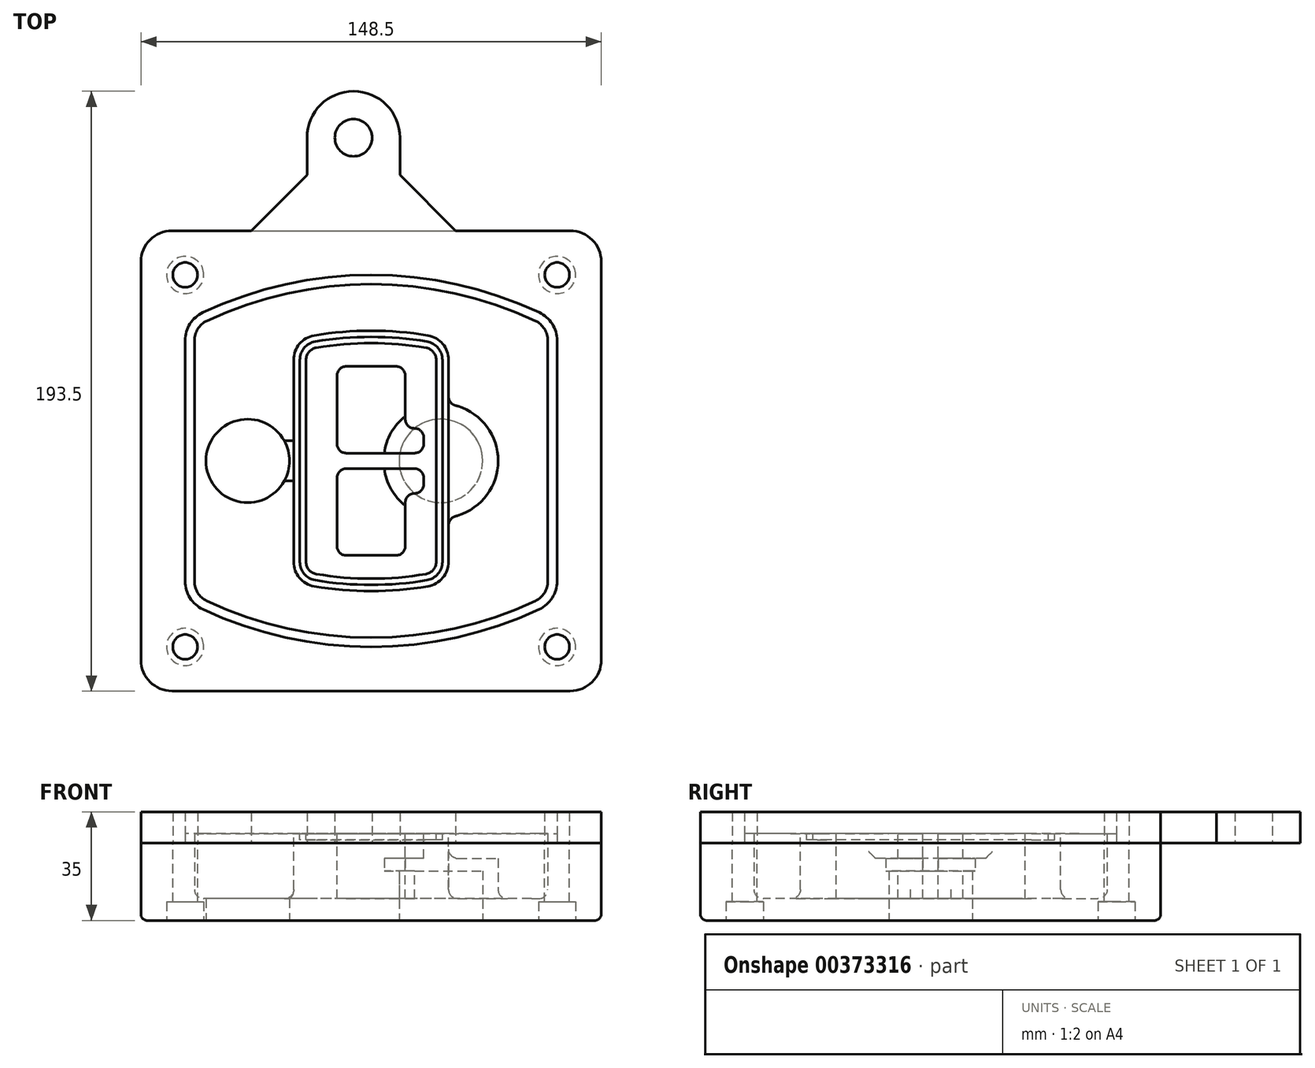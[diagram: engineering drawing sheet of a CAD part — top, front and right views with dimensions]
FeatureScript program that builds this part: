
annotation { "Feature Type Name" : "Feature", "Feature Type Description" : "" }
export const myFeature = defineFeature(function(context is Context, id is Id, definition is map)
    precondition{}
    {
        {
            var Q0;
            Q0=qCreatedBy(makeId("Top.planeOp"),FACE);
            var sketch = newSketch(context, id + "F0", { "sketchPlane" : qUnion([Q0])});
            skPoint(sketch, "E0.rect.middle", {"position": v(0, 0) * mm});
            skLineSegment(sketch, "E1.bottom", {"start": v(-64.25, -74.25) * mm, "end": v(64.25, -74.25) * mm});
            skLineSegment(sketch, "E1.top", {"start": v(-64.25, 74.25) * mm, "end": v(64.25, 74.25) * mm});
            skLineSegment(sketch, "E1.left", {"start": v(-74.25, -64.25) * mm, "end": v(-74.25, 64.25) * mm});
            skLineSegment(sketch, "E1.right", {"start": v(74.25, -64.25) * mm, "end": v(74.25, 64.25) * mm});
            skLineSegment(sketch, "E2", {"start": v(-74.25, 74.25) * mm, "end": v(74.25, -74.25) * mm, "construction": true});
            skLineSegment(sketch, "E3", {"start": v(74.25, 74.25) * mm, "end": v(-74.25, -74.25) * mm, "construction": true});
            skCircle(sketch, "E4", {"center": v(-60, 60) * mm, "radius": 4 * mm});
            skCircle(sketch, "E5", {"center": v(60, 60) * mm, "radius": 4 * mm});
            skCircle(sketch, "E6", {"center": v(60, -60) * mm, "radius": 4 * mm});
            skCircle(sketch, "E7", {"center": v(-60, -60) * mm, "radius": 4 * mm});
            skLineSegment(sketch, "E8", {"start": v(-60, 60) * mm, "end": v(60, 60) * mm, "construction": true});
            skLineSegment(sketch, "E9", {"start": v(60, 60) * mm, "end": v(60, -60) * mm, "construction": true});
            skLineSegment(sketch, "E10", {"start": v(60, -60) * mm, "end": v(-60, -60) * mm, "construction": true});
            skLineSegment(sketch, "E11", {"start": v(-60, -60) * mm, "end": v(-60, 60) * mm, "construction": true});
            skLineSegment(sketch, "E12", {"start": v(-60, 38.83) * mm, "end": v(-60, -38.83) * mm});
            skLineSegment(sketch, "E13", {"start": v(60, 38.83) * mm, "end": v(60, -38.83) * mm});
            skArc(sketch, "E14", {"start": v(54.26, 47.88) * mm, "mid": v(0, 60) * mm, "end": v(-54.26, 47.88) * mm});
            skArc(sketch, "E15", {"start": v(-54.26, -47.88) * mm, "mid": v(0, -60) * mm, "end": v(54.26, -47.88) * mm});
            skLineSegment(sketch, "E16", {"start": v(-60, 0) * mm, "end": v(60, 0) * mm, "construction": true});
            skPoint(sketch, "E17.visualSharp", {"position": v(-60, -45) * mm});
            skArc(sketch, "E17.filletArc", {"start": v(-60, -38.83) * mm, "mid": v(-58.44, -44.2) * mm, "end": v(-54.26, -47.88) * mm});
            skPoint(sketch, "E18.visualSharp", {"position": v(-60, 45) * mm});
            skArc(sketch, "E18.filletArc", {"start": v(-54.26, 47.88) * mm, "mid": v(-58.44, 44.2) * mm, "end": v(-60, 38.83) * mm});
            skPoint(sketch, "E19.visualSharp", {"position": v(60, 45) * mm});
            skArc(sketch, "E19.filletArc", {"start": v(60, 38.83) * mm, "mid": v(58.44, 44.2) * mm, "end": v(54.26, 47.88) * mm});
            skPoint(sketch, "E20.visualSharp", {"position": v(60, -45) * mm});
            skArc(sketch, "E20.filletArc", {"start": v(54.26, -47.88) * mm, "mid": v(58.44, -44.2) * mm, "end": v(60, -38.83) * mm});
            skPoint(sketch, "E21.visualSharp", {"position": v(-74.25, 74.25) * mm});
            skArc(sketch, "E21.filletArc", {"start": v(-64.25, 74.25) * mm, "mid": v(-71.32, 71.32) * mm, "end": v(-74.25, 64.25) * mm});
            skPoint(sketch, "E22.visualSharp", {"position": v(74.25, 74.25) * mm});
            skArc(sketch, "E22.filletArc", {"start": v(74.25, 64.25) * mm, "mid": v(71.32, 71.32) * mm, "end": v(64.25, 74.25) * mm});
            skPoint(sketch, "E23.visualSharp", {"position": v(74.25, -74.25) * mm});
            skArc(sketch, "E23.filletArc", {"start": v(64.25, -74.25) * mm, "mid": v(71.32, -71.32) * mm, "end": v(74.25, -64.25) * mm});
            skPoint(sketch, "E24.visualSharp", {"position": v(-74.25, -74.25) * mm});
            skArc(sketch, "E24.filletArc", {"start": v(-74.25, -64.25) * mm, "mid": v(-71.32, -71.32) * mm, "end": v(-64.25, -74.25) * mm});
            skArc(sketch, "E25.0", {"start": v(57, 38.83) * mm, "mid": v(55.9, 42.58) * mm, "end": v(52.98, 45.17) * mm});
            skLineSegment(sketch, "E25.1", {"start": v(57, 38.83) * mm, "end": v(57, -38.83) * mm});
            skArc(sketch, "E25.2", {"start": v(52.98, -45.17) * mm, "mid": v(55.9, -42.58) * mm, "end": v(57, -38.83) * mm});
            skArc(sketch, "E25.3", {"start": v(-52.98, -45.17) * mm, "mid": v(0, -57) * mm, "end": v(52.98, -45.17) * mm});
            skArc(sketch, "E25.4", {"start": v(-57, -38.83) * mm, "mid": v(-55.9, -42.58) * mm, "end": v(-52.98, -45.17) * mm});
            skArc(sketch, "E25.5", {"start": v(52.98, 45.17) * mm, "mid": v(0, 57) * mm, "end": v(-52.98, 45.17) * mm});
            skLineSegment(sketch, "E25.6", {"start": v(-57, 38.83) * mm, "end": v(-57, -38.83) * mm});
            skArc(sketch, "E25.7", {"start": v(-52.98, 45.17) * mm, "mid": v(-55.9, 42.58) * mm, "end": v(-57, 38.83) * mm});
            skArc(sketch, "E26.0", {"start": v(-55.96, 51.5) * mm, "mid": v(-61.82, 46.33) * mm, "end": v(-64, 38.83) * mm});
            skArc(sketch, "E26.1", {"start": v(55.96, 51.5) * mm, "mid": v(0, 64) * mm, "end": v(-55.96, 51.5) * mm});
            skArc(sketch, "E26.2", {"start": v(64, 38.83) * mm, "mid": v(61.82, 46.33) * mm, "end": v(55.96, 51.5) * mm});
            skLineSegment(sketch, "E26.3", {"start": v(64, 38.83) * mm, "end": v(64, -38.83) * mm});
            skArc(sketch, "E26.4", {"start": v(55.96, -51.5) * mm, "mid": v(61.82, -46.33) * mm, "end": v(64, -38.83) * mm});
            skLineSegment(sketch, "E26.5", {"start": v(-64, 38.83) * mm, "end": v(-64, -38.83) * mm});
            skArc(sketch, "E26.6", {"start": v(-55.96, -51.5) * mm, "mid": v(0, -64) * mm, "end": v(55.96, -51.5) * mm});
            skArc(sketch, "E26.7", {"start": v(-64, -38.83) * mm, "mid": v(-61.82, -46.33) * mm, "end": v(-55.96, -51.5) * mm});
            skSolve(sketch);
        }
        {
            var Q0;
            Q0=makeQuery(id+"F0.imprint","IMPRINT",FACE,{"disambiguationData":[TD([[makeQuery(id+"F0.imprint","IMPRINT",EDGE,{"derivedFrom":sQuery(id+"F0.wireOp",EDGE,"E1.bottom")}),1.0]])]});
            var Q1;
            Q1=makeQuery(id+"F0.imprint","IMPRINT",FACE,{"disambiguationData":[TD([[makeQuery(id+"F0.imprint","IMPRINT",EDGE,{"derivedFrom":sQuery(id+"F0.wireOp",EDGE,"E12")}),1.0]])]});
            var Q2;
            Q2=makeQuery(id+"F0.imprint","IMPRINT",FACE,{"disambiguationData":[TD([[makeQuery(id+"F0.imprint","IMPRINT",EDGE,{"derivedFrom":sQuery(id+"F0.wireOp",EDGE,"E25.0")}),1.0]])]});
            var Q3;
            Q3=makeQuery(id+"F0.imprint","IMPRINT",FACE,{"disambiguationData":[TD([[makeQuery(id+"F0.imprint","IMPRINT",EDGE,{"derivedFrom":sQuery(id+"F0.wireOp",EDGE,"E12")}),-1.0]])]});
            extrude(context, id + "F1", {"entities" : qUnion([Q0, Q1, Q2, Q3]), "oppositeDirection" : true, "depth" : 25 * mm});
        }
        {
            var Q0;
            Q0=makeQuery(id+"F0.imprint","IMPRINT",FACE,{"disambiguationData":[TD([[makeQuery(id+"F0.imprint","IMPRINT",EDGE,{"derivedFrom":sQuery(id+"F0.wireOp",EDGE,"E12")}),1.0]])]});
            extrude(context, id + "F2", {"entities" : qUnion([Q0]), "operationType" : NewBodyOperationType.ADD, "depth" : 3 * mm});
        }
        {
            var Q0;
            Q0=makeQuery(id+"F0.imprint","IMPRINT",FACE,{"disambiguationData":[TD([[makeQuery(id+"F0.imprint","IMPRINT",EDGE,{"derivedFrom":sQuery(id+"F0.wireOp",EDGE,"E25.0")}),1.0]])]});
            extrude(context, id + "F3", {"entities" : qUnion([Q0]), "operationType" : NewBodyOperationType.REMOVE, "oppositeDirection" : true, "depth" : 18 * mm});
        }
        {
            var Q0;
            Q0=makeQuery(id+"F2.opExtrude","CAP_FACE",FACE,{"disambiguationData":[OSD([sQuery(id+"F0.wireOp",EDGE,"E12"),sQuery(id+"F0.wireOp",EDGE,"E13"),sQuery(id+"F0.wireOp",EDGE,"E14"),sQuery(id+"F0.wireOp",EDGE,"E15"),sQuery(id+"F0.wireOp",EDGE,"E17.filletArc"),sQuery(id+"F0.wireOp",EDGE,"E18.filletArc"),sQuery(id+"F0.wireOp",EDGE,"E19.filletArc"),sQuery(id+"F0.wireOp",EDGE,"E20.filletArc"),sQuery(id+"F0.wireOp",EDGE,"E25.0"),sQuery(id+"F0.wireOp",EDGE,"E25.1"),sQuery(id+"F0.wireOp",EDGE,"E25.2"),sQuery(id+"F0.wireOp",EDGE,"E25.3"),sQuery(id+"F0.wireOp",EDGE,"E25.4"),sQuery(id+"F0.wireOp",EDGE,"E25.5"),sQuery(id+"F0.wireOp",EDGE,"E25.6"),sQuery(id+"F0.wireOp",EDGE,"E25.7")])],"isStart":false});
            var sketch = newSketch(context, id + "F4", { "sketchPlane" : qUnion([Q0])});
            skArc(sketch, "E27.0", {"start": v(-18.34, -40.45) * mm, "mid": v(0, -42) * mm, "end": v(18.34, -40.45) * mm});
            skArc(sketch, "E28.0", {"start": v(18.34, 40.45) * mm, "mid": v(0, 42) * mm, "end": v(-18.34, 40.45) * mm});
            skLineSegment(sketch, "E29", {"start": v(-25, 32.57) * mm, "end": v(-25, -32.57) * mm});
            skLineSegment(sketch, "E30", {"start": v(25, 32.57) * mm, "end": v(25, -32.57) * mm});
            skLineSegment(sketch, "E31", {"start": v(-25, 39.1) * mm, "end": v(25, 39.1) * mm, "construction": true});
            skLineSegment(sketch, "E32", {"start": v(-25, -39.1) * mm, "end": v(25, -39.1) * mm, "construction": true});
            skPoint(sketch, "E33.visualSharp", {"position": v(-25, 39.1) * mm});
            skArc(sketch, "E33.filletArc", {"start": v(-18.34, 40.45) * mm, "mid": v(-23.11, 37.73) * mm, "end": v(-25, 32.57) * mm});
            skPoint(sketch, "E34.visualSharp", {"position": v(25, 39.1) * mm});
            skArc(sketch, "E34.filletArc", {"start": v(25, 32.57) * mm, "mid": v(23.11, 37.73) * mm, "end": v(18.34, 40.45) * mm});
            skPoint(sketch, "E35.visualSharp", {"position": v(25, -39.1) * mm});
            skArc(sketch, "E35.filletArc", {"start": v(18.34, -40.45) * mm, "mid": v(23.11, -37.73) * mm, "end": v(25, -32.57) * mm});
            skPoint(sketch, "E36.visualSharp", {"position": v(-25, -39.1) * mm});
            skArc(sketch, "E36.filletArc", {"start": v(-25, -32.57) * mm, "mid": v(-23.11, -37.73) * mm, "end": v(-18.34, -40.45) * mm});
            skArc(sketch, "E37.0", {"start": v(52.98, 45.17) * mm, "mid": v(0, 57) * mm, "end": v(-52.98, 45.17) * mm});
            skArc(sketch, "E37.1", {"start": v(-52.98, 45.17) * mm, "mid": v(-55.9, 42.58) * mm, "end": v(-57, 38.83) * mm});
            skLineSegment(sketch, "E37.2", {"start": v(-57, 38.83) * mm, "end": v(-57, -38.83) * mm});
            skArc(sketch, "E37.3", {"start": v(-57, -38.83) * mm, "mid": v(-55.9, -42.58) * mm, "end": v(-52.98, -45.17) * mm});
            skArc(sketch, "E37.4", {"start": v(-52.98, -45.17) * mm, "mid": v(0, -57) * mm, "end": v(52.98, -45.17) * mm});
            skArc(sketch, "E37.5", {"start": v(52.98, -45.17) * mm, "mid": v(55.9, -42.58) * mm, "end": v(57, -38.83) * mm});
            skLineSegment(sketch, "E37.6", {"start": v(57, 38.83) * mm, "end": v(57, -38.83) * mm});
            skArc(sketch, "E37.7", {"start": v(57, 38.83) * mm, "mid": v(55.9, 42.58) * mm, "end": v(52.98, 45.17) * mm});
            skLineSegment(sketch, "E38.0", {"start": v(23, 32.57) * mm, "end": v(23, -32.57) * mm});
            skArc(sketch, "E38.1", {"start": v(18, -38.48) * mm, "mid": v(21.58, -36.44) * mm, "end": v(23, -32.57) * mm});
            skArc(sketch, "E38.2", {"start": v(-18, -38.48) * mm, "mid": v(0, -40) * mm, "end": v(18, -38.48) * mm});
            skArc(sketch, "E38.3", {"start": v(-23, -32.57) * mm, "mid": v(-21.58, -36.44) * mm, "end": v(-18, -38.48) * mm});
            skLineSegment(sketch, "E38.4", {"start": v(-23, 32.57) * mm, "end": v(-23, -32.57) * mm});
            skArc(sketch, "E38.5", {"start": v(23, 32.57) * mm, "mid": v(21.58, 36.44) * mm, "end": v(18, 38.48) * mm});
            skArc(sketch, "E38.6", {"start": v(-18, 38.48) * mm, "mid": v(-21.58, 36.44) * mm, "end": v(-23, 32.57) * mm});
            skArc(sketch, "E38.7", {"start": v(18, 38.48) * mm, "mid": v(0, 40) * mm, "end": v(-18, 38.48) * mm});
            skArc(sketch, "E39.0", {"start": v(21, 32.57) * mm, "mid": v(20.06, 35.15) * mm, "end": v(17.67, 36.5) * mm});
            skLineSegment(sketch, "E39.1", {"start": v(21, 32.57) * mm, "end": v(21, -32.57) * mm});
            skArc(sketch, "E39.2", {"start": v(17.67, -36.5) * mm, "mid": v(20.06, -35.15) * mm, "end": v(21, -32.57) * mm});
            skArc(sketch, "E39.3", {"start": v(-17.67, -36.5) * mm, "mid": v(0, -38) * mm, "end": v(17.67, -36.5) * mm});
            skArc(sketch, "E39.4", {"start": v(-21, -32.57) * mm, "mid": v(-20.06, -35.15) * mm, "end": v(-17.67, -36.5) * mm});
            skArc(sketch, "E39.5", {"start": v(17.67, 36.5) * mm, "mid": v(0, 38) * mm, "end": v(-17.67, 36.5) * mm});
            skLineSegment(sketch, "E39.6", {"start": v(-21, 32.57) * mm, "end": v(-21, -32.57) * mm});
            skArc(sketch, "E39.7", {"start": v(-17.67, 36.5) * mm, "mid": v(-20.06, 35.15) * mm, "end": v(-21, 32.57) * mm});
            skLineSegment(sketch, "E40", {"start": v(-25, 0) * mm, "end": v(25, 0) * mm, "construction": true});
            skLineSegment(sketch, "E41", {"start": v(-11, 5.5) * mm, "end": v(-11, 27.5) * mm});
            skLineSegment(sketch, "E42", {"start": v(-8, 30.5) * mm, "end": v(8, 30.5) * mm});
            skLineSegment(sketch, "E43", {"start": v(11, 27.5) * mm, "end": v(11, 13.5) * mm});
            skLineSegment(sketch, "E44", {"start": v(14, 10.5) * mm, "end": v(14, 10.5) * mm});
            skLineSegment(sketch, "E45", {"start": v(17, 7.5) * mm, "end": v(17, 5.5) * mm});
            skLineSegment(sketch, "E46", {"start": v(14, 2.5) * mm, "end": v(-8, 2.5) * mm});
            skPoint(sketch, "E47.visualSharp", {"position": v(-11, 30.5) * mm});
            skArc(sketch, "E47.filletArc", {"start": v(-8, 30.5) * mm, "mid": v(-10.12, 29.62) * mm, "end": v(-11, 27.5) * mm});
            skPoint(sketch, "E48.visualSharp", {"position": v(11, 30.5) * mm});
            skArc(sketch, "E48.filletArc", {"start": v(11, 27.5) * mm, "mid": v(10.12, 29.62) * mm, "end": v(8, 30.5) * mm});
            skPoint(sketch, "E49.visualSharp", {"position": v(11, 10.5) * mm});
            skArc(sketch, "E49.filletArc", {"start": v(11, 13.5) * mm, "mid": v(11.88, 11.38) * mm, "end": v(14, 10.5) * mm});
            skPoint(sketch, "E50.visualSharp", {"position": v(17, 10.5) * mm});
            skArc(sketch, "E50.filletArc", {"start": v(17, 7.5) * mm, "mid": v(16.12, 9.62) * mm, "end": v(14, 10.5) * mm});
            skPoint(sketch, "E51.visualSharp", {"position": v(17, 2.5) * mm});
            skArc(sketch, "E51.filletArc", {"start": v(14, 2.5) * mm, "mid": v(16.12, 3.38) * mm, "end": v(17, 5.5) * mm});
            skPoint(sketch, "E52.visualSharp", {"position": v(-11, 2.5) * mm});
            skArc(sketch, "E52.filletArc", {"start": v(-11, 5.5) * mm, "mid": v(-10.12, 3.38) * mm, "end": v(-8, 2.5) * mm});
            skLineSegment(sketch, "E53.0.MirrorCS", {"start": v(14, -2.5) * mm, "end": v(-8, -2.5) * mm});
            skArc(sketch, "E54.0.MirrorCS", {"start": v(-11, -5.5) * mm, "mid": v(-10.12, -3.38) * mm, "end": v(-8, -2.5) * mm});
            skLineSegment(sketch, "E55.0.MirrorCS", {"start": v(-11, -5.5) * mm, "end": v(-11, -27.5) * mm});
            skArc(sketch, "E56.0.MirrorCS", {"start": v(-8, -30.5) * mm, "mid": v(-10.12, -29.62) * mm, "end": v(-11, -27.5) * mm});
            skLineSegment(sketch, "E57.0.MirrorCS", {"start": v(-8, -30.5) * mm, "end": v(8, -30.5) * mm});
            skArc(sketch, "E58.0.MirrorCS", {"start": v(11, -27.5) * mm, "mid": v(10.12, -29.62) * mm, "end": v(8, -30.5) * mm});
            skLineSegment(sketch, "E59.0.MirrorCS", {"start": v(11, -27.5) * mm, "end": v(11, -13.5) * mm});
            skArc(sketch, "E60.0.MirrorCS", {"start": v(11, -13.5) * mm, "mid": v(11.88, -11.38) * mm, "end": v(14, -10.5) * mm});
            skArc(sketch, "E61.0.MirrorCS", {"start": v(17, -7.5) * mm, "mid": v(16.12, -9.62) * mm, "end": v(14, -10.5) * mm});
            skLineSegment(sketch, "E62.0.MirrorCS", {"start": v(17, -7.5) * mm, "end": v(17, -5.5) * mm});
            skArc(sketch, "E63.0.MirrorCS", {"start": v(14, -2.5) * mm, "mid": v(16.12, -3.38) * mm, "end": v(17, -5.5) * mm});
            skSolve(sketch);
        }
        {
            var Q0;
            Q0=makeQuery(id+"F4.imprint","IMPRINT",FACE,{"disambiguationData":[TD([[makeQuery(id+"F4.imprint","IMPRINT",EDGE,{"derivedFrom":sQuery(id+"F4.wireOp",EDGE,"E27.0")}),1.0]])]});
            var Q1;
            Q1=makeQuery(id+"F4.imprint","IMPRINT",FACE,{"disambiguationData":[TD([[makeQuery(id+"F4.imprint","IMPRINT",EDGE,{"derivedFrom":sQuery(id+"F4.wireOp",EDGE,"E38.0")}),-1.0]])]});
            var Q2;
            Q2=makeQuery(id+"F4.imprint","IMPRINT",FACE,{"disambiguationData":[TD([[makeQuery(id+"F4.imprint","IMPRINT",EDGE,{"derivedFrom":sQuery(id+"F4.wireOp",EDGE,"E39.0")}),1.0]])]});
            extrude(context, id + "F5", {"entities" : qUnion([Q0, Q1, Q2]), "operationType" : NewBodyOperationType.ADD, "endBound" : BoundingType.UP_TO_NEXT, "oppositeDirection" : true, "depth" : 25 * mm});
        }
        {
            var Q0;
            Q0=makeQuery(id+"F4.imprint","IMPRINT",FACE,{"disambiguationData":[TD([[makeQuery(id+"F4.imprint","IMPRINT",EDGE,{"derivedFrom":sQuery(id+"F4.wireOp",EDGE,"E38.0")}),-1.0]])]});
            extrude(context, id + "F6", {"entities" : qUnion([Q0]), "operationType" : NewBodyOperationType.REMOVE, "oppositeDirection" : true, "depth" : 2 * mm});
        }
        {
            var Q0;
            Q0=makeQuery(id+"F1.opExtrude","CAP_FACE",FACE,{"disambiguationData":[OSD([sQuery(id+"F0.wireOp",EDGE,"E1.bottom"),sQuery(id+"F0.wireOp",EDGE,"E1.top"),sQuery(id+"F0.wireOp",EDGE,"E1.left"),sQuery(id+"F0.wireOp",EDGE,"E1.right"),sQuery(id+"F0.wireOp",EDGE,"E4"),sQuery(id+"F0.wireOp",EDGE,"E5"),sQuery(id+"F0.wireOp",EDGE,"E6"),sQuery(id+"F0.wireOp",EDGE,"E7"),sQuery(id+"F0.wireOp",EDGE,"E21.filletArc"),sQuery(id+"F0.wireOp",EDGE,"E22.filletArc"),sQuery(id+"F0.wireOp",EDGE,"E23.filletArc"),sQuery(id+"F0.wireOp",EDGE,"E24.filletArc")])],"isStart":false});
            var sketch = newSketch(context, id + "F7", { "sketchPlane" : qUnion([Q0])});
            skCircle(sketch, "E64", {"center": v(22.5, 0) * mm, "radius": 13.47 * mm});
            skCircle(sketch, "E65", {"center": v(-39.81, 0) * mm, "radius": 13.47 * mm});
            skLineSegment(sketch, "E66", {"start": v(74.25, 0) * mm, "end": v(-74.25, 0) * mm});
            skCircle(sketch, "E67", {"center": v(22.5, 0) * mm, "radius": 18.47 * mm});
            skCircle(sketch, "E68", {"center": v(60, -60) * mm, "radius": 6 * mm});
            skCircle(sketch, "E69", {"center": v(-60, -60) * mm, "radius": 6 * mm});
            skCircle(sketch, "E70", {"center": v(-60, 60) * mm, "radius": 6 * mm});
            skCircle(sketch, "E71", {"center": v(60, 60) * mm, "radius": 6 * mm});
            skSolve(sketch);
        }
        {
            var Q0;
            {var subQ1=sQuery(id+"F7.wireOp",EDGE,"E66");var subQ4=sQuery(id+"F7.wireOp",EDGE,"E64");var subQ6=makeQuery(id+"F7.imprint","INTERSECT",VERTEX,{"disambiguationData":[OD(0.0)],"derivedFrom":[subQ4,subQ1]});Q0=makeQuery(id+"F7.imprint","IMPRINT",FACE,{"disambiguationData":[TD([[makeQuery(id+"F7.imprint","IMPRINT",EDGE,{"disambiguationData":[TD([[subQ6,-1.0]])],"derivedFrom":subQ4}),-1.0]])]});}
            var Q1;
            {var subQ0=sQuery(id+"F7.wireOp",EDGE,"E66");var subQ1=sQuery(id+"F7.wireOp",EDGE,"E64");var subQ3=makeQuery(id+"F7.imprint","INTERSECT",VERTEX,{"disambiguationData":[OD(0.0)],"derivedFrom":[subQ1,subQ0]});Q1=makeQuery(id+"F7.imprint","IMPRINT",FACE,{"disambiguationData":[TD([[makeQuery(id+"F7.imprint","IMPRINT",EDGE,{"disambiguationData":[TD([[subQ3,-1.0]])],"derivedFrom":subQ1}),1.0]])]});}
            var Q2;
            {var subQ0=sQuery(id+"F7.wireOp",EDGE,"E66");var subQ1=sQuery(id+"F7.wireOp",EDGE,"E64");var subQ3=makeQuery(id+"F7.imprint","INTERSECT",VERTEX,{"disambiguationData":[OD(0.0)],"derivedFrom":[subQ1,subQ0]});Q2=makeQuery(id+"F7.imprint","IMPRINT",FACE,{"disambiguationData":[TD([[makeQuery(id+"F7.imprint","IMPRINT",EDGE,{"disambiguationData":[TD([[subQ3,1.0]])],"derivedFrom":subQ1}),1.0]])]});}
            var Q3;
            {var subQ1=sQuery(id+"F7.wireOp",EDGE,"E66");var subQ4=sQuery(id+"F7.wireOp",EDGE,"E64");var subQ6=makeQuery(id+"F7.imprint","INTERSECT",VERTEX,{"disambiguationData":[OD(0.0)],"derivedFrom":[subQ4,subQ1]});Q3=makeQuery(id+"F7.imprint","IMPRINT",FACE,{"disambiguationData":[TD([[makeQuery(id+"F7.imprint","IMPRINT",EDGE,{"disambiguationData":[TD([[subQ6,1.0]])],"derivedFrom":subQ4}),-1.0]])]});}
            extrude(context, id + "F8", {"entities" : qUnion([Q0, Q1, Q2, Q3]), "operationType" : NewBodyOperationType.ADD, "oppositeDirection" : true, "depth" : 20 * mm});
        }
        {
            var Q0;
            {var subQ0=sQuery(id+"F7.wireOp",EDGE,"E66");var subQ1=sQuery(id+"F7.wireOp",EDGE,"E64");var subQ3=makeQuery(id+"F7.imprint","INTERSECT",VERTEX,{"disambiguationData":[OD(0.0)],"derivedFrom":[subQ1,subQ0]});Q0=makeQuery(id+"F7.imprint","IMPRINT",FACE,{"disambiguationData":[TD([[makeQuery(id+"F7.imprint","IMPRINT",EDGE,{"disambiguationData":[TD([[subQ3,-1.0]])],"derivedFrom":subQ1}),1.0]])]});}
            var Q1;
            {var subQ0=sQuery(id+"F7.wireOp",EDGE,"E66");var subQ1=sQuery(id+"F7.wireOp",EDGE,"E64");var subQ3=makeQuery(id+"F7.imprint","INTERSECT",VERTEX,{"disambiguationData":[OD(0.0)],"derivedFrom":[subQ1,subQ0]});Q1=makeQuery(id+"F7.imprint","IMPRINT",FACE,{"disambiguationData":[TD([[makeQuery(id+"F7.imprint","IMPRINT",EDGE,{"disambiguationData":[TD([[subQ3,1.0]])],"derivedFrom":subQ1}),1.0]])]});}
            extrude(context, id + "F9", {"entities" : qUnion([Q0, Q1]), "operationType" : NewBodyOperationType.REMOVE, "oppositeDirection" : true, "depth" : 16 * mm});
        }
        {
            var Q0;
            {var subQ0=sQuery(id+"F7.wireOp",EDGE,"E66");var subQ1=sQuery(id+"F7.wireOp",EDGE,"E65");var subQ3=makeQuery(id+"F7.imprint","INTERSECT",VERTEX,{"disambiguationData":[OD(0.0)],"derivedFrom":[subQ1,subQ0]});Q0=makeQuery(id+"F7.imprint","IMPRINT",FACE,{"disambiguationData":[TD([[makeQuery(id+"F7.imprint","IMPRINT",EDGE,{"disambiguationData":[TD([[subQ3,-1.0]])],"derivedFrom":subQ1}),1.0]])]});}
            var Q1;
            {var subQ0=sQuery(id+"F7.wireOp",EDGE,"E66");var subQ1=sQuery(id+"F7.wireOp",EDGE,"E65");var subQ3=makeQuery(id+"F7.imprint","INTERSECT",VERTEX,{"disambiguationData":[OD(0.0)],"derivedFrom":[subQ1,subQ0]});Q1=makeQuery(id+"F7.imprint","IMPRINT",FACE,{"disambiguationData":[TD([[makeQuery(id+"F7.imprint","IMPRINT",EDGE,{"disambiguationData":[TD([[subQ3,1.0]])],"derivedFrom":subQ1}),1.0]])]});}
            extrude(context, id + "F10", {"entities" : qUnion([Q0, Q1]), "operationType" : NewBodyOperationType.REMOVE, "oppositeDirection" : true, "depth" : 25 * mm});
        }
        {
            var Q0;
            Q0=makeQuery(id+"F7.imprint","IMPRINT",FACE,{"disambiguationData":[TD([[makeQuery(id+"F7.imprint","IMPRINT",EDGE,{"derivedFrom":sQuery(id+"F7.wireOp",EDGE,"E68")}),1.0]])]});
            var Q1;
            Q1=makeQuery(id+"F7.imprint","IMPRINT",FACE,{"disambiguationData":[TD([[makeQuery(id+"F7.imprint","IMPRINT",EDGE,{"derivedFrom":makeQuery(id+"F1.opExtrude","CAP_EDGE",EDGE,{"disambiguationData":[OSD([sQuery(id+"F0.wireOp",EDGE,"E5")])],"isStart":false})}),-1.0]])]});
            var Q2;
            Q2=makeQuery(id+"F7.imprint","IMPRINT",FACE,{"disambiguationData":[TD([[makeQuery(id+"F7.imprint","IMPRINT",EDGE,{"derivedFrom":sQuery(id+"F7.wireOp",EDGE,"E69")}),1.0]])]});
            var Q3;
            Q3=makeQuery(id+"F7.imprint","IMPRINT",FACE,{"disambiguationData":[TD([[makeQuery(id+"F7.imprint","IMPRINT",EDGE,{"derivedFrom":makeQuery(id+"F1.opExtrude","CAP_EDGE",EDGE,{"disambiguationData":[OSD([sQuery(id+"F0.wireOp",EDGE,"E4")])],"isStart":false})}),-1.0]])]});
            var Q4;
            Q4=makeQuery(id+"F7.imprint","IMPRINT",FACE,{"disambiguationData":[TD([[makeQuery(id+"F7.imprint","IMPRINT",EDGE,{"derivedFrom":sQuery(id+"F7.wireOp",EDGE,"E70")}),1.0]])]});
            var Q5;
            Q5=makeQuery(id+"F7.imprint","IMPRINT",FACE,{"disambiguationData":[TD([[makeQuery(id+"F7.imprint","IMPRINT",EDGE,{"derivedFrom":makeQuery(id+"F1.opExtrude","CAP_EDGE",EDGE,{"disambiguationData":[OSD([sQuery(id+"F0.wireOp",EDGE,"E7")])],"isStart":false})}),-1.0]])]});
            var Q6;
            Q6=makeQuery(id+"F7.imprint","IMPRINT",FACE,{"disambiguationData":[TD([[makeQuery(id+"F7.imprint","IMPRINT",EDGE,{"derivedFrom":sQuery(id+"F7.wireOp",EDGE,"E71")}),1.0]])]});
            var Q7;
            Q7=makeQuery(id+"F7.imprint","IMPRINT",FACE,{"disambiguationData":[TD([[makeQuery(id+"F7.imprint","IMPRINT",EDGE,{"derivedFrom":makeQuery(id+"F1.opExtrude","CAP_EDGE",EDGE,{"disambiguationData":[OSD([sQuery(id+"F0.wireOp",EDGE,"E6")])],"isStart":false})}),-1.0]])]});
            extrude(context, id + "F11", {"entities" : qUnion([Q0, Q1, Q2, Q3, Q4, Q5, Q6, Q7]), "operationType" : NewBodyOperationType.REMOVE, "oppositeDirection" : true, "depth" : 6 * mm});
        }
        {
            var Q0;
            Q0=makeQuery(id+"F9.boolean.opBoolean","COPY",FACE,{"derivedFrom":makeQuery(id+"F9.opExtrude","CAP_FACE",FACE,{"disambiguationData":[OSD([sQuery(id+"F7.wireOp",EDGE,"E64")])],"isStart":false})});
            var sketch = newSketch(context, id + "F12", { "sketchPlane" : qUnion([Q0])});
            skArc(sketch, "E72.0", {"start": v(11, 14.45) * mm, "mid": v(6.45, 9.13) * mm, "end": v(4.2, 2.5) * mm});
            skArc(sketch, "E72.1", {"start": v(4.2, -2.5) * mm, "mid": v(6.45, -9.13) * mm, "end": v(11, -14.45) * mm});
            skLineSegment(sketch, "E73", {"start": v(4.2, -2.5) * mm, "end": v(14, -2.5) * mm});
            skLineSegment(sketch, "E74.0", {"start": v(14, 2.5) * mm, "end": v(4.2, 2.5) * mm});
            skArc(sketch, "E74.1", {"start": v(14, 2.5) * mm, "mid": v(16.12, 3.38) * mm, "end": v(17, 5.5) * mm});
            skLineSegment(sketch, "E74.2", {"start": v(17, 7.5) * mm, "end": v(17, 5.5) * mm});
            skArc(sketch, "E74.3", {"start": v(17, 7.5) * mm, "mid": v(16.12, 9.62) * mm, "end": v(14, 10.5) * mm});
            skArc(sketch, "E74.4", {"start": v(11, 13.5) * mm, "mid": v(11.88, 11.38) * mm, "end": v(14, 10.5) * mm});
            skLineSegment(sketch, "E74.5", {"start": v(11, 14.45) * mm, "end": v(11, 13.5) * mm});
            skLineSegment(sketch, "E74.7", {"start": v(14, -2.5) * mm, "end": v(4.2, -2.5) * mm});
            skArc(sketch, "E74.8", {"start": v(14, -2.5) * mm, "mid": v(16.12, -3.38) * mm, "end": v(17, -5.5) * mm});
            skLineSegment(sketch, "E74.9", {"start": v(17, -7.5) * mm, "end": v(17, -5.5) * mm});
            skArc(sketch, "E74.10", {"start": v(17, -7.5) * mm, "mid": v(16.12, -9.62) * mm, "end": v(14, -10.5) * mm});
            skArc(sketch, "E74.11", {"start": v(11, -13.5) * mm, "mid": v(11.88, -11.38) * mm, "end": v(14, -10.5) * mm});
            skLineSegment(sketch, "E74.12", {"start": v(11, -14.45) * mm, "end": v(11, -13.5) * mm});
            skPoint(sketch, "E75.orphan", {"position": v(11, -27.5) * mm});
            skPoint(sketch, "E76.orphan", {"position": v(-8, -2.5) * mm});
            skPoint(sketch, "E77.orphan", {"position": v(-8, 2.5) * mm});
            skPoint(sketch, "E78.orphan", {"position": v(11, 27.5) * mm});
            skSolve(sketch);
        }
        {
            var Q0;
            {var subQ7=sQuery(id+"F12.wireOp",EDGE,"E72.0");var subQ14=sQuery(id+"F12.wireOp",EDGE,"E72.1");var subQ16=sQuery(id+"F12.wireOp",EDGE,"E74.1");var subQ18=sQuery(id+"F12.wireOp",EDGE,"E74.8");Q0=qUnion([makeQuery(id+"F12.imprint","IMPRINT",FACE,{"disambiguationData":[TD([[makeQuery(id+"F12.imprint","IMPRINT",EDGE,{"derivedFrom":subQ7}),1.0]])]}),makeQuery(id+"F12.imprint","IMPRINT",FACE,{"disambiguationData":[TD([[makeQuery(id+"F12.imprint","IMPRINT",EDGE,{"derivedFrom":subQ14}),1.0]])]}),makeQuery(id+"F12.imprint","IMPRINT",FACE,{"disambiguationData":[TD([[makeQuery(id+"F12.imprint","IMPRINT",EDGE,{"derivedFrom":subQ16}),1.0]])]}),makeQuery(id+"F12.imprint","IMPRINT",FACE,{"disambiguationData":[TD([[makeQuery(id+"F12.imprint","IMPRINT",EDGE,{"derivedFrom":subQ18}),-1.0]])]})]);}
            var Q1;
            Q1=makeQuery(id+"F5.boolean.opBoolean","SPLIT",FACE,{"disambiguationData":[TD([makeQuery(id+"F5.opExtrude","SWEPT_FACE",FACE,{"disambiguationData":[OSD([sQuery(id+"F4.wireOp",EDGE,"E41")])]})])],"derivedFrom":makeQuery(id+"F3.boolean.opBoolean","COPY",FACE,{"derivedFrom":makeQuery(id+"F3.opExtrude","CAP_FACE",FACE,{"disambiguationData":[OSD([sQuery(id+"F0.wireOp",EDGE,"E25.0"),sQuery(id+"F0.wireOp",EDGE,"E25.1"),sQuery(id+"F0.wireOp",EDGE,"E25.2"),sQuery(id+"F0.wireOp",EDGE,"E25.3"),sQuery(id+"F0.wireOp",EDGE,"E25.4"),sQuery(id+"F0.wireOp",EDGE,"E25.5"),sQuery(id+"F0.wireOp",EDGE,"E25.6"),sQuery(id+"F0.wireOp",EDGE,"E25.7")])],"isStart":false})})});
            extrude(context, id + "F13", {"entities" : qUnion([Q0]), "operationType" : NewBodyOperationType.REMOVE, "endBound" : BoundingType.UP_TO_SURFACE, "endBoundEntityFace" : qUnion([Q1]), "depth" : 25 * mm});
        }
        {
            var Q0;
            Q0=makeQuery(id+"F3.boolean.opBoolean","COPY",EDGE,{"derivedFrom":makeQuery(id+"F3.opExtrude","CAP_EDGE",EDGE,{"disambiguationData":[OSD([sQuery(id+"F0.wireOp",EDGE,"E25.6")])],"isStart":false})});
            var Q1;
            Q1=makeQuery(id+"F8.boolean.opBoolean","INTERSECT",EDGE,{"derivedFrom":[makeQuery(id+"F5.opExtrude","SWEPT_FACE",FACE,{"disambiguationData":[OSD([sQuery(id+"F4.wireOp",EDGE,"E30")])]}),makeQuery(id+"F8.opExtrude","CAP_FACE",FACE,{"disambiguationData":[OSD([sQuery(id+"F7.wireOp",EDGE,"E67")])],"isStart":false})]});
            var Q2;
            Q2=makeQuery(id+"F8.boolean.opBoolean","INTERSECT",EDGE,{"disambiguationData":[OD(1.0)],"derivedFrom":[makeQuery(id+"F5.opExtrude","SWEPT_FACE",FACE,{"disambiguationData":[OSD([sQuery(id+"F4.wireOp",EDGE,"E30")])]}),makeQuery(id+"F8.opExtrude","SWEPT_FACE",FACE,{"disambiguationData":[OSD([sQuery(id+"F7.wireOp",EDGE,"E67")])]})]});
            var Q3;
            {var subQ0=sQuery(id+"F4.wireOp",EDGE,"E30");Q3=makeQuery(id+"F8.boolean.opBoolean","SPLIT",EDGE,{"disambiguationData":[TD([makeQuery(id+"F5.opExtrude","SWEPT_FACE",FACE,{"disambiguationData":[OSD([sQuery(id+"F4.wireOp",EDGE,"E35.filletArc")])]})])],"derivedFrom":makeQuery(id+"F5.opExtrude","CAP_EDGE",EDGE,{"disambiguationData":[OSD([subQ0])],"isStart":false})});}
            var Q4;
            {var subQ0=sQuery(id+"F0.wireOp",EDGE,"E25.7");var subQ1=sQuery(id+"F0.wireOp",EDGE,"E25.1");var subQ2=sQuery(id+"F0.wireOp",EDGE,"E25.6");var subQ3=sQuery(id+"F0.wireOp",EDGE,"E25.5");var subQ4=sQuery(id+"F0.wireOp",EDGE,"E25.4");var subQ5=sQuery(id+"F0.wireOp",EDGE,"E25.0");var subQ6=sQuery(id+"F0.wireOp",EDGE,"E25.2");var subQ7=sQuery(id+"F0.wireOp",EDGE,"E25.3");Q4=makeQuery(id+"F8.boolean.opBoolean","INTERSECT",EDGE,{"derivedFrom":[makeQuery(id+"F5.boolean.opBoolean","SPLIT",FACE,{"disambiguationData":[TD([makeQuery(id+"F2.opExtrude","SWEPT_FACE",FACE,{"disambiguationData":[OSD([subQ5])]})])],"derivedFrom":makeQuery(id+"F3.boolean.opBoolean","COPY",FACE,{"derivedFrom":makeQuery(id+"F3.opExtrude","CAP_FACE",FACE,{"disambiguationData":[OSD([subQ5,subQ1,subQ6,subQ7,subQ4,subQ3,subQ2,subQ0])],"isStart":false})})}),makeQuery(id+"F8.opExtrude","SWEPT_FACE",FACE,{"disambiguationData":[OSD([sQuery(id+"F7.wireOp",EDGE,"E67")])]})]});}
            var Q5;
            Q5=makeQuery(id+"F8.boolean.opBoolean","INTERSECT",EDGE,{"disambiguationData":[OD(0.0)],"derivedFrom":[makeQuery(id+"F5.opExtrude","SWEPT_FACE",FACE,{"disambiguationData":[OSD([sQuery(id+"F4.wireOp",EDGE,"E30")])]}),makeQuery(id+"F8.opExtrude","SWEPT_FACE",FACE,{"disambiguationData":[OSD([sQuery(id+"F7.wireOp",EDGE,"E67")])]})]});
            fillet(context, id + "F14", {"entities" : qUnion([Q0, Q1, Q2, Q3, Q4, Q5]), "radius" : 3 * mm, "tangentPropagation" : true, "allowEdgeOverflow" : false});
        }
        {
            var Q0;
            Q0=makeQuery(id+"F1.opExtrude","CAP_EDGE",EDGE,{"disambiguationData":[OSD([sQuery(id+"F0.wireOp",EDGE,"E1.bottom")])],"isStart":false});
            fillet(context, id + "F15", {"entities" : qUnion([Q0]), "radius" : 2 * mm, "tangentPropagation" : true, "allowEdgeOverflow" : false});
        }
        {
            var Q0;
            {var subQ0=sQuery(id+"F0.wireOp",EDGE,"E21.filletArc");var subQ1=sQuery(id+"F0.wireOp",EDGE,"E7");var subQ2=sQuery(id+"F0.wireOp",EDGE,"E6");var subQ3=sQuery(id+"F0.wireOp",EDGE,"E5");var subQ4=sQuery(id+"F0.wireOp",EDGE,"E4");var subQ5=sQuery(id+"F0.wireOp",EDGE,"E22.filletArc");var subQ6=sQuery(id+"F0.wireOp",EDGE,"E1.bottom");var subQ7=sQuery(id+"F0.wireOp",EDGE,"E1.right");var subQ8=sQuery(id+"F0.wireOp",EDGE,"E1.top");var subQ9=sQuery(id+"F0.wireOp",EDGE,"E1.left");var subQ10=sQuery(id+"F0.wireOp",EDGE,"E23.filletArc");var subQ11=sQuery(id+"F0.wireOp",EDGE,"E24.filletArc");Q0=makeQuery(id+"F2.boolean.opBoolean","SPLIT",FACE,{"disambiguationData":[TD([makeQuery(id+"F1.opExtrude","SWEPT_FACE",FACE,{"disambiguationData":[OSD([subQ6])]})])],"derivedFrom":makeQuery(id+"F1.opExtrude","CAP_FACE",FACE,{"disambiguationData":[OSD([subQ6,subQ8,subQ9,subQ7,subQ4,subQ3,subQ2,subQ1,subQ0,subQ5,subQ10,subQ11])],"isStart":true})});}
            var sketch = newSketch(context, id + "F16", { "sketchPlane" : qUnion([Q0])});
            skArc(sketch, "E79", {"start": v(9.3, 104.25) * mm, "mid": v(-5.7, 119.25) * mm, "end": v(-20.7, 104.25) * mm});
            skLineSegment(sketch, "E80", {"start": v(-20.7, 104.25) * mm, "end": v(-20.7, 92.25) * mm});
            skLineSegment(sketch, "E81", {"start": v(9.3, 104.25) * mm, "end": v(9.3, 92.25) * mm});
            skLineSegment(sketch, "E82", {"start": v(-20.7, 92.25) * mm, "end": v(-38.7, 74.25) * mm});
            skLineSegment(sketch, "E83", {"start": v(9.3, 92.25) * mm, "end": v(27.3, 74.25) * mm});
            skCircle(sketch, "E84", {"center": v(-5.7, 104.25) * mm, "radius": 6 * mm});
            skArc(sketch, "E85.MirrorCS", {"start": v(9.3, -104.25) * mm, "mid": v(-5.7, -119.25) * mm, "end": v(-20.7, -104.25) * mm});
            skLineSegment(sketch, "E86.MirrorCS", {"start": v(-20.7, -104.25) * mm, "end": v(-20.7, -92.25) * mm});
            skCircle(sketch, "E87.MirrorC", {"center": v(-5.7, -104.25) * mm, "radius": 6 * mm});
            skLineSegment(sketch, "E88.MirrorCS", {"start": v(9.3, -92.25) * mm, "end": v(27.3, -74.25) * mm});
            skLineSegment(sketch, "E89.MirrorCS", {"start": v(9.3, -104.25) * mm, "end": v(9.3, -92.25) * mm});
            skLineSegment(sketch, "E90.MirrorCS", {"start": v(-20.7, -92.25) * mm, "end": v(-38.7, -74.25) * mm});
            skSolve(sketch);
        }
        {
            var Q0;
            Q0=makeQuery(id+"F16.imprint","IMPRINT",FACE,{"disambiguationData":[TD([[makeQuery(id+"F16.imprint","IMPRINT",EDGE,{"derivedFrom":sQuery(id+"F16.wireOp",EDGE,"E79")}),1.0]])]});
            var Q1;
            Q1=makeQuery(id+"F16.imprint","IMPRINT",FACE,{"disambiguationData":[TD([[makeQuery(id+"F16.imprint","IMPRINT",EDGE,{"derivedFrom":sQuery(id+"F16.wireOp",EDGE,"E85.MirrorCS")}),-1.0]])]});
            var Q2;
            Q2=makeQuery(id+"F16.imprint","IMPRINT",FACE,{"disambiguationData":[TD([[makeQuery(id+"F16.imprint","IMPRINT",EDGE,{"derivedFrom":makeQuery(id+"F1.opExtrude","CAP_EDGE",EDGE,{"disambiguationData":[OSD([sQuery(id+"F0.wireOp",EDGE,"E1.left")])],"isStart":true})}),-1.0]])]});
            extrude(context, id + "F17", {"entities" : qUnion([Q0, Q1, Q2]), "depth" : 10 * mm});
        }
    });
